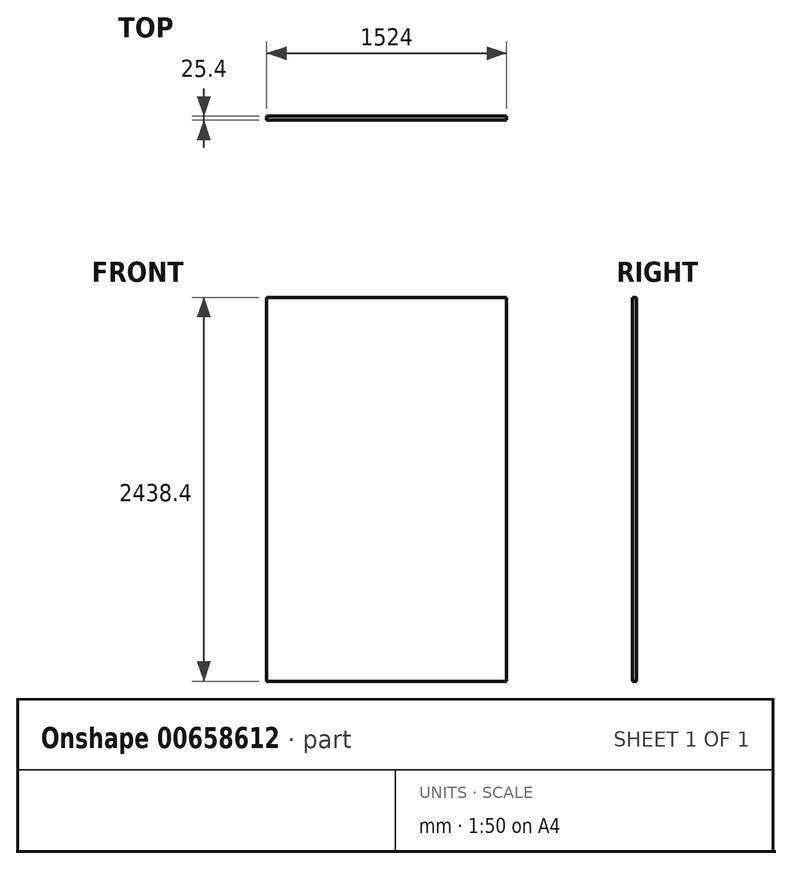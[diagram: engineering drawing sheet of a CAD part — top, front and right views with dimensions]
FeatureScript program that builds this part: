
annotation { "Feature Type Name" : "Feature", "Feature Type Description" : "" }
export const myFeature = defineFeature(function(context is Context, id is Id, definition is map)
    precondition{}
    {
        {
            var Q0;
            Q0=qCreatedBy(makeId("Front.planeOp"),FACE);
            var sketch = newSketch(context, id + "F0", { "sketchPlane" : qUnion([Q0])});
            skLineSegment(sketch, "E0.bottom", {"start": v(762, 1219.2) * mm, "end": v(-762, 1219.2) * mm});
            skLineSegment(sketch, "E0.top", {"start": v(762, -1219.2) * mm, "end": v(-762, -1219.2) * mm});
            skLineSegment(sketch, "E0.left", {"start": v(762, 1219.2) * mm, "end": v(762, -1219.2) * mm});
            skLineSegment(sketch, "E0.right", {"start": v(-762, 1219.2) * mm, "end": v(-762, -1219.2) * mm});
            skPoint(sketch, "E0.middle", {"position": v(0, 0) * mm});
            skSolve(sketch);
        }
        {
            var Q0;
            Q0=makeQuery(id+"F0.imprint","IMPRINT",FACE,{"disambiguationData":[TD([[makeQuery(id+"F0.imprint","IMPRINT",EDGE,{"derivedFrom":sQuery(id+"F0.wireOp",EDGE,"E0.bottom")}),1.0]])]});
            extrude(context, id + "F1", {"entities" : qUnion([Q0]), "depth" : 25.4 * mm, "offsetDistance" : 25.4 * mm});
        }
    });
